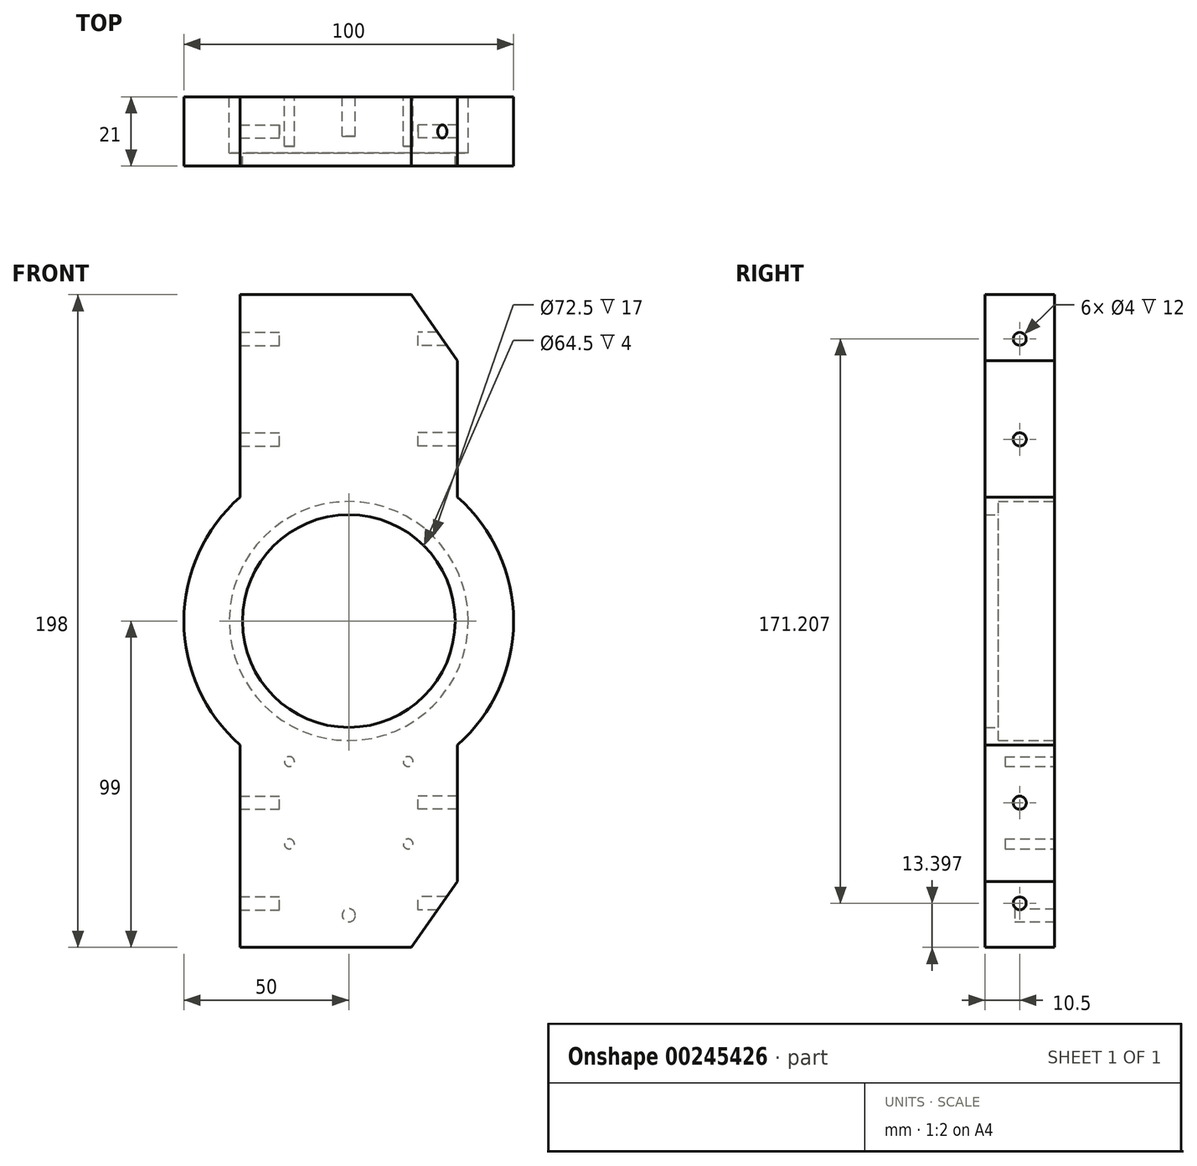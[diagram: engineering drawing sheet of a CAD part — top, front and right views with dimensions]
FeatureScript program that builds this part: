
annotation { "Feature Type Name" : "Feature", "Feature Type Description" : "" }
export const myFeature = defineFeature(function(context is Context, id is Id, definition is map)
    precondition{}
    {
        {
            var Q0;
            Q0=qCreatedBy(makeId("Front.planeOp"),FACE);
            var sketch = newSketch(context, id + "F0", { "sketchPlane" : qUnion([Q0])});
            skCircle(sketch, "E0", {"center": v(0, 0) * mm, "radius": 36.25 * mm});
            skPoint(sketch, "E1.endSnap0", {"position": v(0, -99) * mm});
            skLineSegment(sketch, "E2.trimOffspring", {"start": v(-19, -99) * mm, "end": v(19, -99) * mm});
            skArc(sketch, "E3.MirrorCS", {"start": v(50, 0) * mm, "mid": v(45.55, -20.62) * mm, "end": v(33, -37.56) * mm});
            skLineSegment(sketch, "E4.trimOffspring", {"start": v(33, -37.56) * mm, "end": v(33, -79) * mm});
            skLineSegment(sketch, "E5.trimOffspring", {"start": v(-33, -37.56) * mm, "end": v(-33, -79) * mm});
            skArc(sketch, "E6.trimOffspring", {"start": v(-33, -37.56) * mm, "mid": v(-45.55, -20.62) * mm, "end": v(-50, 0) * mm});
            skLineSegment(sketch, "E7", {"start": v(0, -99) * mm, "end": v(0, -81.4) * mm});
            skLineSegment(sketch, "E8.MirrorCS", {"start": v(33, -79) * mm, "end": v(19, -99) * mm});
            skLineSegment(sketch, "E9", {"start": v(-19, -99) * mm, "end": v(-33, -99) * mm});
            skLineSegment(sketch, "E10", {"start": v(-33, -99) * mm, "end": v(-33, -79) * mm});
            skLineSegment(sketch, "E11", {"start": v(0, 0) * mm, "end": v(-16.88, 0) * mm});
            skArc(sketch, "E12.MirrorCS", {"start": v(-33, 37.56) * mm, "mid": v(-45.55, 20.62) * mm, "end": v(-50, 0) * mm});
            skArc(sketch, "E13.MirrorCS", {"start": v(50, 0) * mm, "mid": v(45.55, 20.62) * mm, "end": v(33, 37.56) * mm});
            skLineSegment(sketch, "E14.MirrorCS", {"start": v(33, 37.56) * mm, "end": v(33, 79) * mm});
            skLineSegment(sketch, "E15.MirrorCS", {"start": v(33, 79) * mm, "end": v(19, 99) * mm});
            skLineSegment(sketch, "E16.MirrorCS", {"start": v(-19, 99) * mm, "end": v(19, 99) * mm});
            skLineSegment(sketch, "E17.MirrorCS", {"start": v(-19, 99) * mm, "end": v(-33, 99) * mm});
            skLineSegment(sketch, "E18.MirrorCS", {"start": v(-33, 99) * mm, "end": v(-33, 79) * mm});
            skLineSegment(sketch, "E19.MirrorCS", {"start": v(-33, 37.56) * mm, "end": v(-33, 79) * mm});
            skSolve(sketch);
        }
        {
            var Q0;
            Q0=qSketchRegion(id+"F0",true);
            extrude(context, id + "F1", {"entities" : qUnion([Q0]), "depth" : 17 * mm});
        }
        {
            var Q0;
            Q0=makeQuery(id+"F1.opExtrude","CAP_FACE",FACE,{"disambiguationData":[OSD([sQuery(id+"F0.wireOp",EDGE,"E0"),sQuery(id+"F0.wireOp",EDGE,"sriAROx1-1mcf-ybja-LQLx-MSVXLM3HJmWQ"),sQuery(id+"F0.wireOp",EDGE,"9Qu72541-LivO-jTMm-oUwD-ZALQE2Hvik1n"),sQuery(id+"F0.wireOp",EDGE,"i4TymV6R-teZx-C7h1-2yMt-q0MvK4pHcOex"),sQuery(id+"F0.wireOp",EDGE,"pD05HJNU-Muf5-boTQ-xGwQ-RlADy1BkldT5")])],"isStart":false});
            var sketch = newSketch(context, id + "F2", { "sketchPlane" : qUnion([Q0])});
            skCircle(sketch, "E20", {"center": v(0, 0) * mm, "radius": 32.25 * mm});
            skLineSegment(sketch, "E21.left", {"start": v(33, -37.56) * mm, "end": v(33, -79) * mm});
            skLineSegment(sketch, "E21.right", {"start": v(-33, -37.56) * mm, "end": v(-33, -37.56) * mm});
            skLineSegment(sketch, "E22", {"start": v(-33, -37.56) * mm, "end": v(-33, -99) * mm});
            skLineSegment(sketch, "E23", {"start": v(33, -79) * mm, "end": v(19, -99) * mm});
            skLineSegment(sketch, "E24", {"start": v(-33, -99) * mm, "end": v(19, -99) * mm});
            skArc(sketch, "E25", {"start": v(33, -37.56) * mm, "mid": v(50, 0) * mm, "end": v(33, 37.56) * mm});
            skLineSegment(sketch, "E26.MirrorCS", {"start": v(33, 37.56) * mm, "end": v(33, 79) * mm});
            skLineSegment(sketch, "E27.MirrorCS", {"start": v(33, 79) * mm, "end": v(19, 99) * mm});
            skLineSegment(sketch, "E28.MirrorCS", {"start": v(-33, 99) * mm, "end": v(19, 99) * mm});
            skLineSegment(sketch, "E29.MirrorCS", {"start": v(-33, 37.56) * mm, "end": v(-33, 99) * mm});
            skArc(sketch, "E30.trimOffspring", {"start": v(-33, 37.56) * mm, "mid": v(-50, 0) * mm, "end": v(-33, -37.56) * mm});
            skSolve(sketch);
        }
        {
            var Q0;
            Q0=qSketchRegion(id+"F2",true);
            extrude(context, id + "F3", {"entities" : qUnion([Q0]), "operationType" : NewBodyOperationType.ADD, "depth" : 4 * mm});
        }
        {
            var Q0;
            Q0=makeQuery(id+"F1.opExtrude","CAP_FACE",FACE,{"disambiguationData":[OSD([sQuery(id+"F0.wireOp",EDGE,"E0"),sQuery(id+"F0.wireOp",EDGE,"sriAROx1-1mcf-ybja-LQLx-MSVXLM3HJmWQ"),sQuery(id+"F0.wireOp",EDGE,"9Qu72541-LivO-jTMm-oUwD-ZALQE2Hvik1n"),sQuery(id+"F0.wireOp",EDGE,"i4TymV6R-teZx-C7h1-2yMt-q0MvK4pHcOex"),sQuery(id+"F0.wireOp",EDGE,"pD05HJNU-Muf5-boTQ-xGwQ-RlADy1BkldT5")])],"isStart":true});
            var sketch = newSketch(context, id + "F4", { "sketchPlane" : qUnion([Q0])});
            skCircle(sketch, "E31", {"center": v(-18, -42.6) * mm, "radius": 1.5 * mm});
            skCircle(sketch, "E32", {"center": v(18, -42.6) * mm, "radius": 1.5 * mm});
            skCircle(sketch, "E33", {"center": v(18, -67.6) * mm, "radius": 1.5 * mm});
            skCircle(sketch, "E34", {"center": v(-18, -67.6) * mm, "radius": 1.5 * mm});
            skSolve(sketch);
        }
        {
            var Q0;
            Q0=qSketchRegion(id+"F4",true);
            extrude(context, id + "F5", {"entities" : qUnion([Q0]), "operationType" : NewBodyOperationType.REMOVE, "oppositeDirection" : true, "depth" : 15 * mm});
        }
        {
            var Q0;
            Q0=qCreatedBy(makeId("Right.planeOp"),FACE);
            cPlane(context, id + "F6", {"entities" : qUnion([Q0]), "cplaneType" : CPlaneType.OFFSET, "offset" : (33 - 12) * mm, "width" : 150 * mm, "height" : 150 * mm});
        }
        {
            var Q0;
            Q0=qCreatedBy(id+"F6.planeOp",FACE);
            var sketch = newSketch(context, id + "F7", { "sketchPlane" : qUnion([Q0])});
            skLineSegment(sketch, "E35", {"start": v(0, 0) * mm, "end": v(0, -42.6) * mm});
            skLineSegment(sketch, "E36", {"start": v(0, -42.6) * mm, "end": v(0, -67.6) * mm});
            skLineSegment(sketch, "E37", {"start": v(0, -67.6) * mm, "end": v(0, -85.6) * mm});
            skLineSegment(sketch, "E38", {"start": v(0, -55.1) * mm, "end": v(-21, -55.1) * mm});
            skLineSegment(sketch, "E39", {"start": v(0, -85.6) * mm, "end": v(-21, -85.6) * mm});
            skCircle(sketch, "E40", {"center": v(-10.5, -55.1) * mm, "radius": 2 * mm});
            skCircle(sketch, "E41", {"center": v(-10.5, -85.6) * mm, "radius": 2 * mm});
            skLineSegment(sketch, "E42", {"start": v(0, 0) * mm, "end": v(-27.37, 0) * mm});
            skCircle(sketch, "E43.MirrorC", {"center": v(-10.5, 55.1) * mm, "radius": 2 * mm});
            skCircle(sketch, "E44.MirrorC", {"center": v(-10.5, 85.6) * mm, "radius": 2 * mm});
            skSolve(sketch);
        }
        {
            var Q0;
            Q0=qSketchRegion(id+"F7",true);
            extrude(context, id + "F8", {"entities" : qUnion([Q0]), "operationType" : NewBodyOperationType.REMOVE, "depth" : 25 * mm});
        }
        {
            var Q0;
            Q0=qCreatedBy(makeId("Right.planeOp"),FACE);
            cPlane(context, id + "F9", {"entities" : qUnion([Q0]), "cplaneType" : CPlaneType.OFFSET, "offset" : (33 - 12) * mm, "oppositeDirection" : true, "width" : 150 * mm, "height" : 150 * mm});
        }
        {
            var Q0;
            Q0=qCreatedBy(id+"F9.planeOp",FACE);
            var sketch = newSketch(context, id + "F10", { "sketchPlane" : qUnion([Q0])});
            skLineSegment(sketch, "E45", {"start": v(0, 0) * mm, "end": v(0, -42.6) * mm});
            skLineSegment(sketch, "E46", {"start": v(0, -42.6) * mm, "end": v(0, -67.6) * mm});
            skLineSegment(sketch, "E47", {"start": v(0, -67.6) * mm, "end": v(0, -85.6) * mm});
            skLineSegment(sketch, "E48", {"start": v(0, -85.6) * mm, "end": v(-21, -85.6) * mm});
            skLineSegment(sketch, "E49", {"start": v(0, -55.1) * mm, "end": v(-21, -55.1) * mm});
            skCircle(sketch, "E50", {"center": v(-10.5, -55.1) * mm, "radius": 2 * mm});
            skCircle(sketch, "E51", {"center": v(-10.5, -85.6) * mm, "radius": 2 * mm});
            skLineSegment(sketch, "E52", {"start": v(0, 0) * mm, "end": v(-33.47, 0) * mm});
            skCircle(sketch, "E53.MirrorC", {"center": v(-10.5, 55.1) * mm, "radius": 2 * mm});
            skCircle(sketch, "E54.MirrorC", {"center": v(-10.5, 85.6) * mm, "radius": 2 * mm});
            skSolve(sketch);
        }
        {
            var Q0;
            Q0=qSketchRegion(id+"F10",true);
            extrude(context, id + "F11", {"entities" : qUnion([Q0]), "operationType" : NewBodyOperationType.REMOVE, "oppositeDirection" : true, "depth" : 25 * mm});
        }
        {
            var Q0;
            Q0=makeQuery(id+"F1.opExtrude","CAP_FACE",FACE,{"disambiguationData":[OSD([sQuery(id+"F0.wireOp",EDGE,"E0"),sQuery(id+"F0.wireOp",EDGE,"E2.trimOffspring"),sQuery(id+"F0.wireOp",EDGE,"E3.MirrorCS"),sQuery(id+"F0.wireOp",EDGE,"E4.trimOffspring"),sQuery(id+"F0.wireOp",EDGE,"E5.trimOffspring"),sQuery(id+"F0.wireOp",EDGE,"E6.trimOffspring"),sQuery(id+"F0.wireOp",EDGE,"E8.MirrorCS"),sQuery(id+"F0.wireOp",EDGE,"E9"),sQuery(id+"F0.wireOp",EDGE,"E10"),sQuery(id+"F0.wireOp",EDGE,"E12.MirrorCS"),sQuery(id+"F0.wireOp",EDGE,"E13.MirrorCS"),sQuery(id+"F0.wireOp",EDGE,"E14.MirrorCS"),sQuery(id+"F0.wireOp",EDGE,"E15.MirrorCS"),sQuery(id+"F0.wireOp",EDGE,"E16.MirrorCS"),sQuery(id+"F0.wireOp",EDGE,"E17.MirrorCS"),sQuery(id+"F0.wireOp",EDGE,"E18.MirrorCS"),sQuery(id+"F0.wireOp",EDGE,"E19.MirrorCS")])],"isStart":true});
            var sketch = newSketch(context, id + "F12", { "sketchPlane" : qUnion([Q0])});
            skLineSegment(sketch, "E55", {"start": v(0, -99) * mm, "end": v(0, -79.5) * mm});
            skCircle(sketch, "E56", {"center": v(0, -89.25) * mm, "radius": 2 * mm});
            skSolve(sketch);
        }
        {
            var Q0;
            Q0=qSketchRegion(id+"F12",true);
            extrude(context, id + "F13", {"entities" : qUnion([Q0]), "operationType" : NewBodyOperationType.REMOVE, "oppositeDirection" : true, "depth" : 12 * mm});
        }
    });
